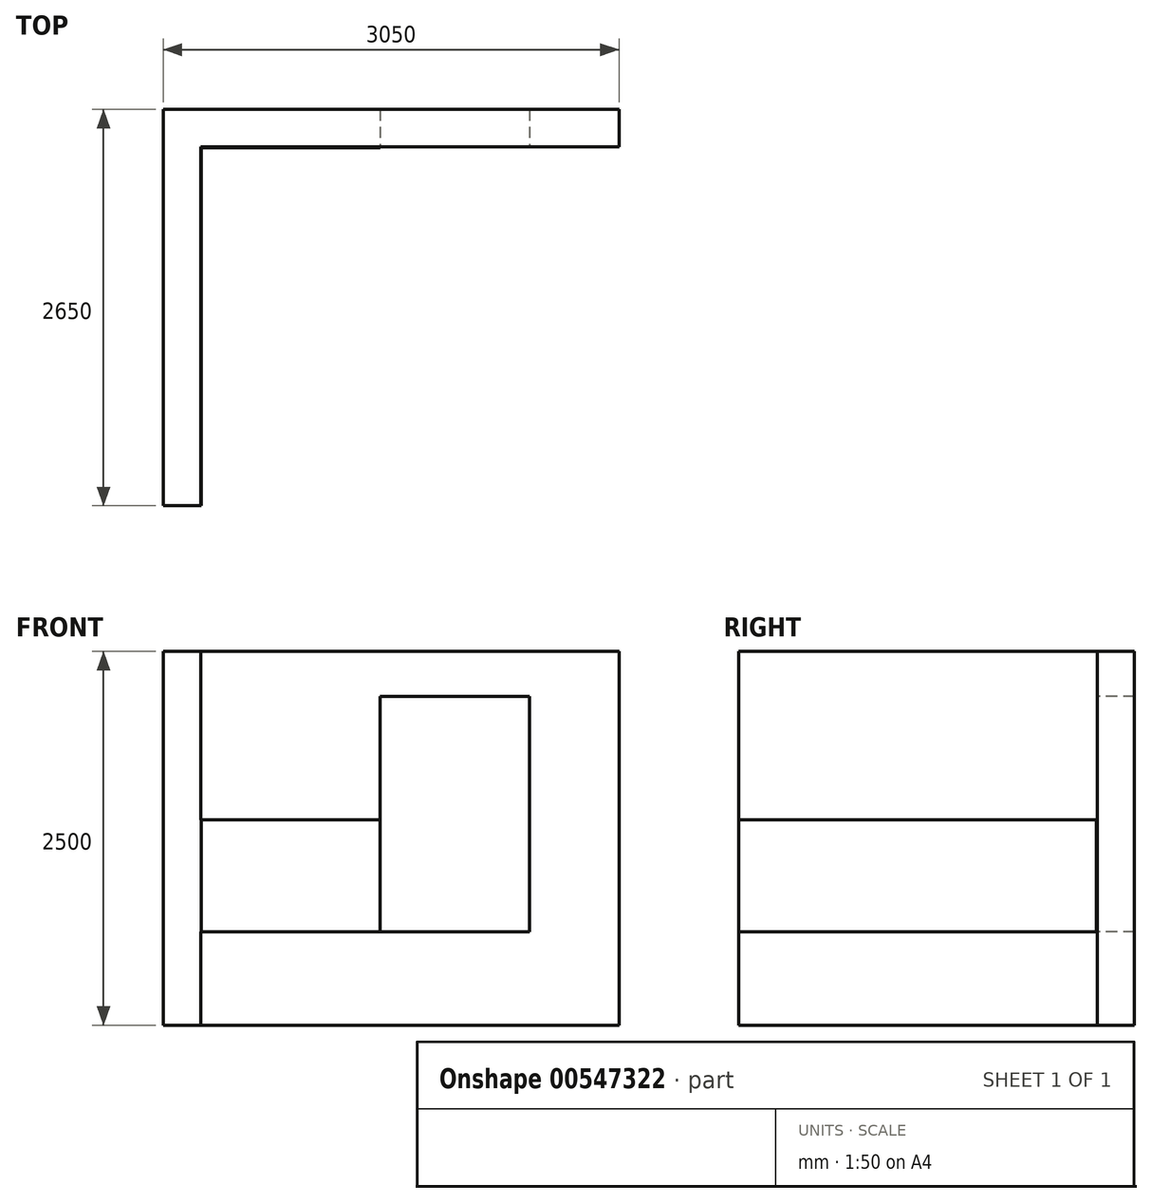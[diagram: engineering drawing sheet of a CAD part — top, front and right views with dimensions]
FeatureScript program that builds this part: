
annotation { "Feature Type Name" : "Feature", "Feature Type Description" : "" }
export const myFeature = defineFeature(function(context is Context, id is Id, definition is map)
    precondition{}
    {
        {
            var Q0;
            Q0=qCreatedBy(makeId("Top.planeOp"),FACE);
            var sketch = newSketch(context, id + "F0", { "sketchPlane" : qUnion([Q0])});
            skLineSegment(sketch, "E0", {"start": v(0, 0) * mm, "end": v(2800, 0) * mm});
            skLineSegment(sketch, "E1", {"start": v(2800, 0) * mm, "end": v(2800, 250) * mm});
            skLineSegment(sketch, "E2", {"start": v(2800, 250) * mm, "end": v(-250, 250) * mm});
            skLineSegment(sketch, "E3", {"start": v(-250, 250) * mm, "end": v(-250, -2400) * mm});
            skLineSegment(sketch, "E4", {"start": v(-250, -2400) * mm, "end": v(0, -2400) * mm});
            skLineSegment(sketch, "E5", {"start": v(0, -2400) * mm, "end": v(0, 0) * mm});
            skSolve(sketch);
        }
        {
            var Q0;
            Q0=makeQuery(id+"F0.imprint","IMPRINT",FACE,{"disambiguationData":[TD([[makeQuery(id+"F0.imprint","IMPRINT",EDGE,{"derivedFrom":sQuery(id+"F0.wireOp",EDGE,"E0")}),1.0]])]});
            extrude(context, id + "F1", {"entities" : qUnion([Q0]), "depth" : 2500 * mm, "offsetDistance" : 25 * mm});
        }
        {
            var Q0;
            Q0=makeQuery(id+"F1.opExtrude","SWEPT_FACE",FACE,{"disambiguationData":[OSD([sQuery(id+"F0.wireOp",EDGE,"E0")])]});
            var sketch = newSketch(context, id + "F2", { "sketchPlane" : qUnion([Q0])});
            skLineSegment(sketch, "E6.bottom", {"start": v(2200, 2200) * mm, "end": v(1200, 2200) * mm});
            skLineSegment(sketch, "E6.top", {"start": v(2200, 625) * mm, "end": v(1200, 625) * mm});
            skLineSegment(sketch, "E6.left", {"start": v(2200, 2200) * mm, "end": v(2200, 625) * mm});
            skLineSegment(sketch, "E6.right", {"start": v(1200, 2200) * mm, "end": v(1200, 625) * mm});
            skSolve(sketch);
        }
        {
            var Q0;
            Q0=makeQuery(id+"F2.imprint","IMPRINT",FACE,{"disambiguationData":[TD([[makeQuery(id+"F2.imprint","IMPRINT",EDGE,{"derivedFrom":sQuery(id+"F2.wireOp",EDGE,"E6.bottom")}),1.0]])]});
            extrude(context, id + "F3", {"entities" : qUnion([Q0]), "operationType" : NewBodyOperationType.REMOVE, "endBound" : BoundingType.THROUGH_ALL, "oppositeDirection" : true, "depth" : 25 * mm, "offsetDistance" : 25 * mm});
        }
        {
            var Q0;
            Q0=makeQuery(id+"F1.opExtrude","SWEPT_FACE",FACE,{"disambiguationData":[OSD([sQuery(id+"F0.wireOp",EDGE,"E0")])]});
            var sketch = newSketch(context, id + "F4", { "sketchPlane" : qUnion([Q0])});
            skLineSegment(sketch, "E7.bottom", {"start": v(1200, 625) * mm, "end": v(0, 625) * mm});
            skLineSegment(sketch, "E7.top", {"start": v(1200, 1375) * mm, "end": v(0, 1375) * mm});
            skLineSegment(sketch, "E7.left", {"start": v(1200, 625) * mm, "end": v(1200, 1375) * mm});
            skLineSegment(sketch, "E7.right", {"start": v(0, 625) * mm, "end": v(0, 1375) * mm});
            skSolve(sketch);
        }
        {
            var Q0;
            Q0=makeQuery(id+"F4.imprint","IMPRINT",FACE,{"disambiguationData":[TD([[makeQuery(id+"F4.imprint","IMPRINT",EDGE,{"derivedFrom":sQuery(id+"F4.wireOp",EDGE,"E7.bottom")}),-1.0]])]});
            extrude(context, id + "F5", {"entities" : qUnion([Q0]), "operationType" : NewBodyOperationType.ADD, "depth" : 5 * mm, "offsetDistance" : 25 * mm});
        }
        {
            var Q0;
            Q0=makeQuery(id+"F1.opExtrude","SWEPT_FACE",FACE,{"disambiguationData":[OSD([sQuery(id+"F0.wireOp",EDGE,"E5")])]});
            var sketch = newSketch(context, id + "F6", { "sketchPlane" : qUnion([Q0])});
            skSolve(sketch);
        }
        {
            var Q0;
            {var subQ2=sQuery(id+"F0.wireOp",EDGE,"E5");Q0=makeQuery(id+"F6.imprint","IMPRINT",FACE,{"disambiguationData":[TD([[makeQuery(id+"F6.imprint","IMPRINT",EDGE,{"derivedFrom":makeQuery(id+"F1.opExtrude","CAP_EDGE",EDGE,{"disambiguationData":[OSD([subQ2])],"isStart":true})}),1.0]])]});}
            var sketch = newSketch(context, id + "F7", { "sketchPlane" : qUnion([Q0])});
            skLineSegment(sketch, "E8.0", {"start": v(-2400, 2500) * mm, "end": v(-2400, 0) * mm});
            skLineSegment(sketch, "E9.bottom", {"start": v(0, 625) * mm, "end": v(-2400, 625) * mm});
            skLineSegment(sketch, "E9.top", {"start": v(0, 1375) * mm, "end": v(-2400, 1375) * mm});
            skLineSegment(sketch, "E9.left", {"start": v(0, 625) * mm, "end": v(0, 1375) * mm});
            skLineSegment(sketch, "E9.right", {"start": v(-2400, 625) * mm, "end": v(-2400, 1375) * mm});
            skSolve(sketch);
        }
        {
            var Q0;
            Q0 = qSketchRegion(id + "F7", true);
            extrude(context, id + "F8", {"entities" : qUnion([Q0]), "operationType" : NewBodyOperationType.ADD, "depth" : 5 * mm, "offsetDistance" : 25 * mm});
        }
    });
